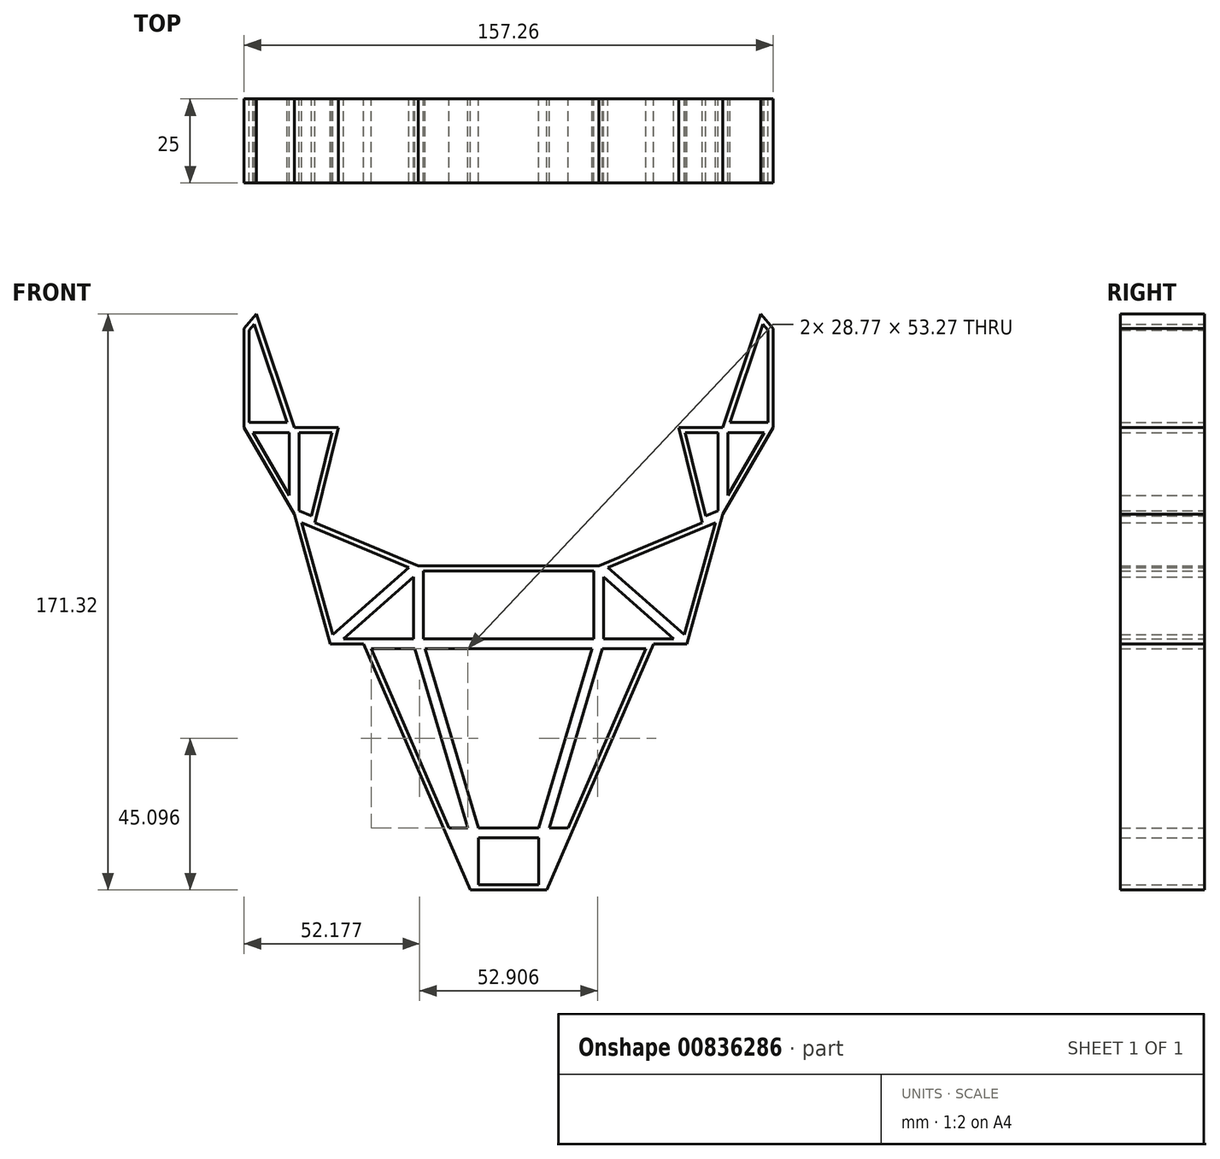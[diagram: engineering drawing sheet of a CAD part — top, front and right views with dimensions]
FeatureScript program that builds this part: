
annotation { "Feature Type Name" : "Feature", "Feature Type Description" : "" }
export const myFeature = defineFeature(function(context is Context, id is Id, definition is map)
    precondition{}
    {
        {
            var Q0;
            Q0=qCreatedBy(makeId("Front.planeOp"),FACE);
            var sketch = newSketch(context, id + "F0", { "sketchPlane" : qUnion([Q0])});
            skLineSegment(sketch, "E0", {"start": v(0, 0) * mm, "end": v(-26.8, 0) * mm});
            skLineSegment(sketch, "E1", {"start": v(-26.8, 0) * mm, "end": v(-26.8, 23.2) * mm});
            skLineSegment(sketch, "E2", {"start": v(-26.8, 23.2) * mm, "end": v(0, 23.2) * mm});
            skLineSegment(sketch, "E3", {"start": v(-26.8, 23.2) * mm, "end": v(-53, 0) * mm});
            skLineSegment(sketch, "E4", {"start": v(-53, 0) * mm, "end": v(-26.8, 0) * mm});
            skLineSegment(sketch, "E5", {"start": v(-26.8, 23.2) * mm, "end": v(-63.74, 38.53) * mm});
            skLineSegment(sketch, "E6", {"start": v(-63.74, 38.53) * mm, "end": v(-53, 0) * mm});
            skLineSegment(sketch, "E7", {"start": v(-26.8, 0) * mm, "end": v(-10.06, -56.27) * mm});
            skLineSegment(sketch, "E8", {"start": v(-10.06, -56.27) * mm, "end": v(0, -56.27) * mm});
            skLineSegment(sketch, "E9", {"start": v(-43.12, 0) * mm, "end": v(-18.7, -56.27) * mm});
            skLineSegment(sketch, "E10", {"start": v(-18.7, -56.27) * mm, "end": v(-10.06, -56.27) * mm});
            skLineSegment(sketch, "E11", {"start": v(-18.7, -56.27) * mm, "end": v(-11.35, -73.23) * mm});
            skLineSegment(sketch, "E12", {"start": v(-11.35, -73.23) * mm, "end": v(0, -73.23) * mm});
            skLineSegment(sketch, "E13.MirrorCS", {"start": v(18.7, -56.27) * mm, "end": v(10.06, -56.27) * mm});
            skLineSegment(sketch, "E14.MirrorCS", {"start": v(78.63, 93.83) * mm, "end": v(75.03, 98.09) * mm});
            skLineSegment(sketch, "E15.MirrorCS", {"start": v(63.74, 38.53) * mm, "end": v(53, 0) * mm});
            skLineSegment(sketch, "E16.MirrorCS", {"start": v(26.8, 0) * mm, "end": v(26.8, 23.2) * mm});
            skLineSegment(sketch, "E17.MirrorCS", {"start": v(78.63, 64.36) * mm, "end": v(78.63, 93.83) * mm});
            skLineSegment(sketch, "E18.MirrorCS", {"start": v(26.8, 23.2) * mm, "end": v(53, 0) * mm});
            skLineSegment(sketch, "E19.MirrorCS", {"start": v(26.8, 0) * mm, "end": v(10.06, -56.27) * mm});
            skLineSegment(sketch, "E20.MirrorCS", {"start": v(26.8, 23.2) * mm, "end": v(63.74, 38.53) * mm});
            skLineSegment(sketch, "E21.MirrorCS", {"start": v(53, 0) * mm, "end": v(26.8, 0) * mm});
            skLineSegment(sketch, "E22.MirrorCS", {"start": v(43.12, 0) * mm, "end": v(18.7, -56.27) * mm});
            skLineSegment(sketch, "E23.MirrorCS", {"start": v(10.06, -56.27) * mm, "end": v(0, -56.27) * mm});
            skLineSegment(sketch, "E24.MirrorCS", {"start": v(26.8, 23.2) * mm, "end": v(0, 23.2) * mm});
            skLineSegment(sketch, "E25.MirrorCS", {"start": v(11.35, -73.23) * mm, "end": v(0, -73.23) * mm});
            skLineSegment(sketch, "E26.MirrorCS", {"start": v(18.7, -56.27) * mm, "end": v(11.35, -73.23) * mm});
            skLineSegment(sketch, "E27.MirrorCS", {"start": v(0, 0) * mm, "end": v(26.8, 0) * mm});
            skLineSegment(sketch, "E28", {"start": v(-25.3, 21.7) * mm, "end": v(-25.3, 1.5) * mm});
            skLineSegment(sketch, "E29", {"start": v(-25.3, 1.5) * mm, "end": v(25.3, 1.5) * mm});
            skLineSegment(sketch, "E30", {"start": v(25.3, 1.5) * mm, "end": v(25.3, 21.7) * mm});
            skLineSegment(sketch, "E31", {"start": v(25.3, 21.7) * mm, "end": v(-25.3, 21.7) * mm});
            skLineSegment(sketch, "E32", {"start": v(28.3, 1.5) * mm, "end": v(49.05, 1.5) * mm});
            skLineSegment(sketch, "E33", {"start": v(49.05, 1.5) * mm, "end": v(28.3, 19.87) * mm});
            skLineSegment(sketch, "E34", {"start": v(28.3, 19.87) * mm, "end": v(28.3, 1.5) * mm});
            skLineSegment(sketch, "E35.MirrorCS", {"start": v(-28.3, 19.87) * mm, "end": v(-28.3, 1.5) * mm});
            skLineSegment(sketch, "E36.MirrorCS", {"start": v(-49.05, 1.5) * mm, "end": v(-28.3, 19.87) * mm});
            skLineSegment(sketch, "E37.MirrorCS", {"start": v(-28.3, 1.5) * mm, "end": v(-49.05, 1.5) * mm});
            skLineSegment(sketch, "E38", {"start": v(29.59, 22.73) * mm, "end": v(52.2, 2.71) * mm});
            skLineSegment(sketch, "E39", {"start": v(52.2, 2.71) * mm, "end": v(61.47, 35.96) * mm});
            skLineSegment(sketch, "E40", {"start": v(61.47, 35.96) * mm, "end": v(29.59, 22.73) * mm});
            skLineSegment(sketch, "E41.MirrorCS", {"start": v(-29.59, 22.73) * mm, "end": v(-52.2, 2.71) * mm});
            skLineSegment(sketch, "E42.MirrorCS", {"start": v(-61.47, 35.96) * mm, "end": v(-29.59, 22.73) * mm});
            skLineSegment(sketch, "E43.MirrorCS", {"start": v(-52.2, 2.71) * mm, "end": v(-61.47, 35.96) * mm});
            skLineSegment(sketch, "E44", {"start": v(62.24, 62.86) * mm, "end": v(52.55, 62.86) * mm});
            skLineSegment(sketch, "E45", {"start": v(65.24, 62.86) * mm, "end": v(76.03, 62.86) * mm});
            skPoint(sketch, "E45.startSnap0", {"position": v(57.4, 62.86) * mm});
            skLineSegment(sketch, "E46", {"start": v(76.03, 62.86) * mm, "end": v(65.24, 44.14) * mm});
            skLineSegment(sketch, "E47", {"start": v(65.24, 44.14) * mm, "end": v(65.24, 62.86) * mm});
            skLineSegment(sketch, "E48", {"start": v(65.83, 65.86) * mm, "end": v(77.13, 65.86) * mm});
            skLineSegment(sketch, "E49", {"start": v(77.13, 65.86) * mm, "end": v(77.13, 93.28) * mm});
            skLineSegment(sketch, "E50", {"start": v(77.13, 93.28) * mm, "end": v(75.6, 95.08) * mm});
            skLineSegment(sketch, "E51", {"start": v(75.6, 95.08) * mm, "end": v(65.83, 65.86) * mm});
            skLineSegment(sketch, "E52", {"start": v(-24.79, -1.5) * mm, "end": v(24.79, -1.5) * mm});
            skLineSegment(sketch, "E53", {"start": v(24.79, -1.5) * mm, "end": v(8.94, -54.77) * mm});
            skLineSegment(sketch, "E54", {"start": v(8.94, -54.77) * mm, "end": v(-8.94, -54.77) * mm});
            skLineSegment(sketch, "E55", {"start": v(-8.94, -54.77) * mm, "end": v(-24.79, -1.5) * mm});
            skLineSegment(sketch, "E56", {"start": v(-8.94, -57.77) * mm, "end": v(-8.94, -71.73) * mm});
            skLineSegment(sketch, "E57", {"start": v(-8.94, -71.73) * mm, "end": v(8.94, -71.73) * mm});
            skLineSegment(sketch, "E58", {"start": v(8.94, -71.73) * mm, "end": v(8.94, -57.77) * mm});
            skLineSegment(sketch, "E59", {"start": v(8.94, -57.77) * mm, "end": v(-8.94, -57.77) * mm});
            skLineSegment(sketch, "E60", {"start": v(50.64, 64.36) * mm, "end": v(57.56, 35.96) * mm});
            skLineSegment(sketch, "E61", {"start": v(57.56, 35.96) * mm, "end": v(63.74, 38.53) * mm});
            skLineSegment(sketch, "E62", {"start": v(52.55, 62.86) * mm, "end": v(58.6, 38.02) * mm});
            skLineSegment(sketch, "E63", {"start": v(58.6, 38.02) * mm, "end": v(62.24, 39.53) * mm});
            skLineSegment(sketch, "E64", {"start": v(62.24, 39.53) * mm, "end": v(62.24, 62.86) * mm});
            skLineSegment(sketch, "E65", {"start": v(-40.84, -1.5) * mm, "end": v(-27.92, -1.5) * mm});
            skLineSegment(sketch, "E66", {"start": v(-27.92, -1.5) * mm, "end": v(-12.07, -54.77) * mm});
            skLineSegment(sketch, "E67", {"start": v(-12.07, -54.77) * mm, "end": v(-17.72, -54.77) * mm});
            skLineSegment(sketch, "E68", {"start": v(-17.72, -54.77) * mm, "end": v(-40.84, -1.5) * mm});
            skLineSegment(sketch, "E69.MirrorCS", {"start": v(12.07, -54.77) * mm, "end": v(17.72, -54.77) * mm});
            skLineSegment(sketch, "E70.MirrorCS", {"start": v(27.92, -1.5) * mm, "end": v(12.07, -54.77) * mm});
            skLineSegment(sketch, "E71.MirrorCS", {"start": v(40.84, -1.5) * mm, "end": v(27.92, -1.5) * mm});
            skLineSegment(sketch, "E72.MirrorCS", {"start": v(17.72, -54.77) * mm, "end": v(40.84, -1.5) * mm});
            skLineSegment(sketch, "E73", {"start": v(63.74, 64.36) * mm, "end": v(78.63, 64.36) * mm});
            skLineSegment(sketch, "E74", {"start": v(63.74, 64.36) * mm, "end": v(75.03, 98.09) * mm});
            skLineSegment(sketch, "E75", {"start": v(63.74, 64.36) * mm, "end": v(50.64, 64.36) * mm});
            skLineSegment(sketch, "E76", {"start": v(63.74, 64.36) * mm, "end": v(63.74, 38.53) * mm});
            skLineSegment(sketch, "E77", {"start": v(78.63, 64.36) * mm, "end": v(63.74, 38.53) * mm});
            skLineSegment(sketch, "E78.MirrorCS", {"start": v(-78.63, 93.83) * mm, "end": v(-75.03, 98.09) * mm});
            skLineSegment(sketch, "E79.MirrorCS", {"start": v(-58.6, 38.02) * mm, "end": v(-62.24, 39.53) * mm});
            skLineSegment(sketch, "E80.MirrorCS", {"start": v(-77.13, 93.28) * mm, "end": v(-75.6, 95.08) * mm});
            skLineSegment(sketch, "E81.MirrorCS", {"start": v(-57.56, 35.96) * mm, "end": v(-63.74, 38.53) * mm});
            skLineSegment(sketch, "E82.MirrorCS", {"start": v(-62.24, 62.86) * mm, "end": v(-52.55, 62.86) * mm});
            skLineSegment(sketch, "E83.MirrorCS", {"start": v(-63.74, 64.36) * mm, "end": v(-50.64, 64.36) * mm});
            skPoint(sketch, "E84.MirrorP", {"position": v(-57.4, 62.86) * mm});
            skLineSegment(sketch, "E85.MirrorCS", {"start": v(-78.63, 64.36) * mm, "end": v(-78.63, 93.83) * mm});
            skLineSegment(sketch, "E86.MirrorCS", {"start": v(-75.6, 95.08) * mm, "end": v(-65.83, 65.86) * mm});
            skLineSegment(sketch, "E87.MirrorCS", {"start": v(-63.74, 64.36) * mm, "end": v(-78.63, 64.36) * mm});
            skLineSegment(sketch, "E88.MirrorCS", {"start": v(-76.03, 62.86) * mm, "end": v(-65.24, 44.14) * mm});
            skLineSegment(sketch, "E89.MirrorCS", {"start": v(-77.13, 65.86) * mm, "end": v(-77.13, 93.28) * mm});
            skLineSegment(sketch, "E90.MirrorCS", {"start": v(-65.83, 65.86) * mm, "end": v(-77.13, 65.86) * mm});
            skLineSegment(sketch, "E91.MirrorCS", {"start": v(-63.74, 64.36) * mm, "end": v(-63.74, 38.53) * mm});
            skLineSegment(sketch, "E92.MirrorCS", {"start": v(-65.24, 62.86) * mm, "end": v(-76.03, 62.86) * mm});
            skLineSegment(sketch, "E93.MirrorCS", {"start": v(-63.74, 64.36) * mm, "end": v(-75.03, 98.09) * mm});
            skLineSegment(sketch, "E94.MirrorCS", {"start": v(-78.63, 64.36) * mm, "end": v(-63.74, 38.53) * mm});
            skLineSegment(sketch, "E95.MirrorCS", {"start": v(-65.24, 44.14) * mm, "end": v(-65.24, 62.86) * mm});
            skLineSegment(sketch, "E96.MirrorCS", {"start": v(-50.64, 64.36) * mm, "end": v(-57.56, 35.96) * mm});
            skLineSegment(sketch, "E97.MirrorCS", {"start": v(-52.55, 62.86) * mm, "end": v(-58.6, 38.02) * mm});
            skLineSegment(sketch, "E98.MirrorCS", {"start": v(-62.24, 39.53) * mm, "end": v(-62.24, 62.86) * mm});
            skSolve(sketch);
        }
        {
            var Q0;
            Q0=makeQuery(id+"F0.imprint","IMPRINT",FACE,{"disambiguationData":[TD([[makeQuery(id+"F0.imprint","IMPRINT",EDGE,{"derivedFrom":sQuery(id+"F0.wireOp",EDGE,"E78.MirrorCS")}),-1.0]])]});
            var Q1;
            Q1=makeQuery(id+"F0.imprint","IMPRINT",FACE,{"disambiguationData":[TD([[makeQuery(id+"F0.imprint","IMPRINT",EDGE,{"derivedFrom":sQuery(id+"F0.wireOp",EDGE,"E87.MirrorCS")}),1.0]])]});
            var Q2;
            Q2=makeQuery(id+"F0.imprint","IMPRINT",FACE,{"disambiguationData":[TD([[makeQuery(id+"F0.imprint","IMPRINT",EDGE,{"derivedFrom":sQuery(id+"F0.wireOp",EDGE,"E79.MirrorCS")}),1.0]])]});
            var Q3;
            Q3=makeQuery(id+"F0.imprint","IMPRINT",FACE,{"disambiguationData":[TD([[makeQuery(id+"F0.imprint","IMPRINT",EDGE,{"derivedFrom":sQuery(id+"F0.wireOp",EDGE,"E3")}),-1.0]])]});
            var Q4;
            {var subQ1=sQuery(id+"F0.wireOp",EDGE,"E1");Q4=makeQuery(id+"F0.imprint","IMPRINT",FACE,{"disambiguationData":[TD([[makeQuery(id+"F0.imprint","IMPRINT",EDGE,{"derivedFrom":subQ1}),1.0]])]});}
            var Q5;
            Q5=makeQuery(id+"F0.imprint","IMPRINT",FACE,{"disambiguationData":[TD([[makeQuery(id+"F0.imprint","IMPRINT",EDGE,{"derivedFrom":sQuery(id+"F0.wireOp",EDGE,"E0")}),-1.0]])]});
            var Q6;
            {var subQ1=sQuery(id+"F0.wireOp",EDGE,"E16.MirrorCS");Q6=makeQuery(id+"F0.imprint","IMPRINT",FACE,{"disambiguationData":[TD([[makeQuery(id+"F0.imprint","IMPRINT",EDGE,{"derivedFrom":subQ1}),-1.0]])]});}
            var Q7;
            Q7=makeQuery(id+"F0.imprint","IMPRINT",FACE,{"disambiguationData":[TD([[makeQuery(id+"F0.imprint","IMPRINT",EDGE,{"derivedFrom":sQuery(id+"F0.wireOp",EDGE,"E15.MirrorCS")}),-1.0]])]});
            var Q8;
            Q8=makeQuery(id+"F0.imprint","IMPRINT",FACE,{"disambiguationData":[TD([[makeQuery(id+"F0.imprint","IMPRINT",EDGE,{"derivedFrom":sQuery(id+"F0.wireOp",EDGE,"E44")}),-1.0]])]});
            var Q9;
            Q9=makeQuery(id+"F0.imprint","IMPRINT",FACE,{"disambiguationData":[TD([[makeQuery(id+"F0.imprint","IMPRINT",EDGE,{"derivedFrom":sQuery(id+"F0.wireOp",EDGE,"E45")}),1.0]])]});
            var Q10;
            Q10=makeQuery(id+"F0.imprint","IMPRINT",FACE,{"disambiguationData":[TD([[makeQuery(id+"F0.imprint","IMPRINT",EDGE,{"derivedFrom":sQuery(id+"F0.wireOp",EDGE,"E14.MirrorCS")}),1.0]])]});
            var Q11;
            Q11=makeQuery(id+"F0.imprint","IMPRINT",FACE,{"disambiguationData":[TD([[makeQuery(id+"F0.imprint","IMPRINT",EDGE,{"derivedFrom":sQuery(id+"F0.wireOp",EDGE,"E0")}),1.0]])]});
            var Q12;
            Q12=makeQuery(id+"F0.imprint","IMPRINT",FACE,{"disambiguationData":[TD([[makeQuery(id+"F0.imprint","IMPRINT",EDGE,{"derivedFrom":sQuery(id+"F0.wireOp",EDGE,"E13.MirrorCS")}),-1.0]])]});
            var Q13;
            {var subQ0=sQuery(id+"F0.wireOp",EDGE,"E7");Q13=makeQuery(id+"F0.imprint","IMPRINT",FACE,{"disambiguationData":[TD([[makeQuery(id+"F0.imprint","IMPRINT",EDGE,{"derivedFrom":subQ0}),-1.0]])]});}
            var Q14;
            Q14=makeQuery(id+"F0.imprint","IMPRINT",FACE,{"disambiguationData":[TD([[makeQuery(id+"F0.imprint","IMPRINT",EDGE,{"derivedFrom":sQuery(id+"F0.wireOp",EDGE,"E8")}),-1.0]])]});
            extrude(context, id + "F1", {"entities" : qUnion([Q0, Q1, Q2, Q3, Q4, Q5, Q6, Q7, Q8, Q9, Q10, Q11, Q12, Q13, Q14]), "endBound" : BoundingType.SYMMETRIC, "depth" : 25 * mm, "offsetDistance" : 25 * mm});
        }
    });
